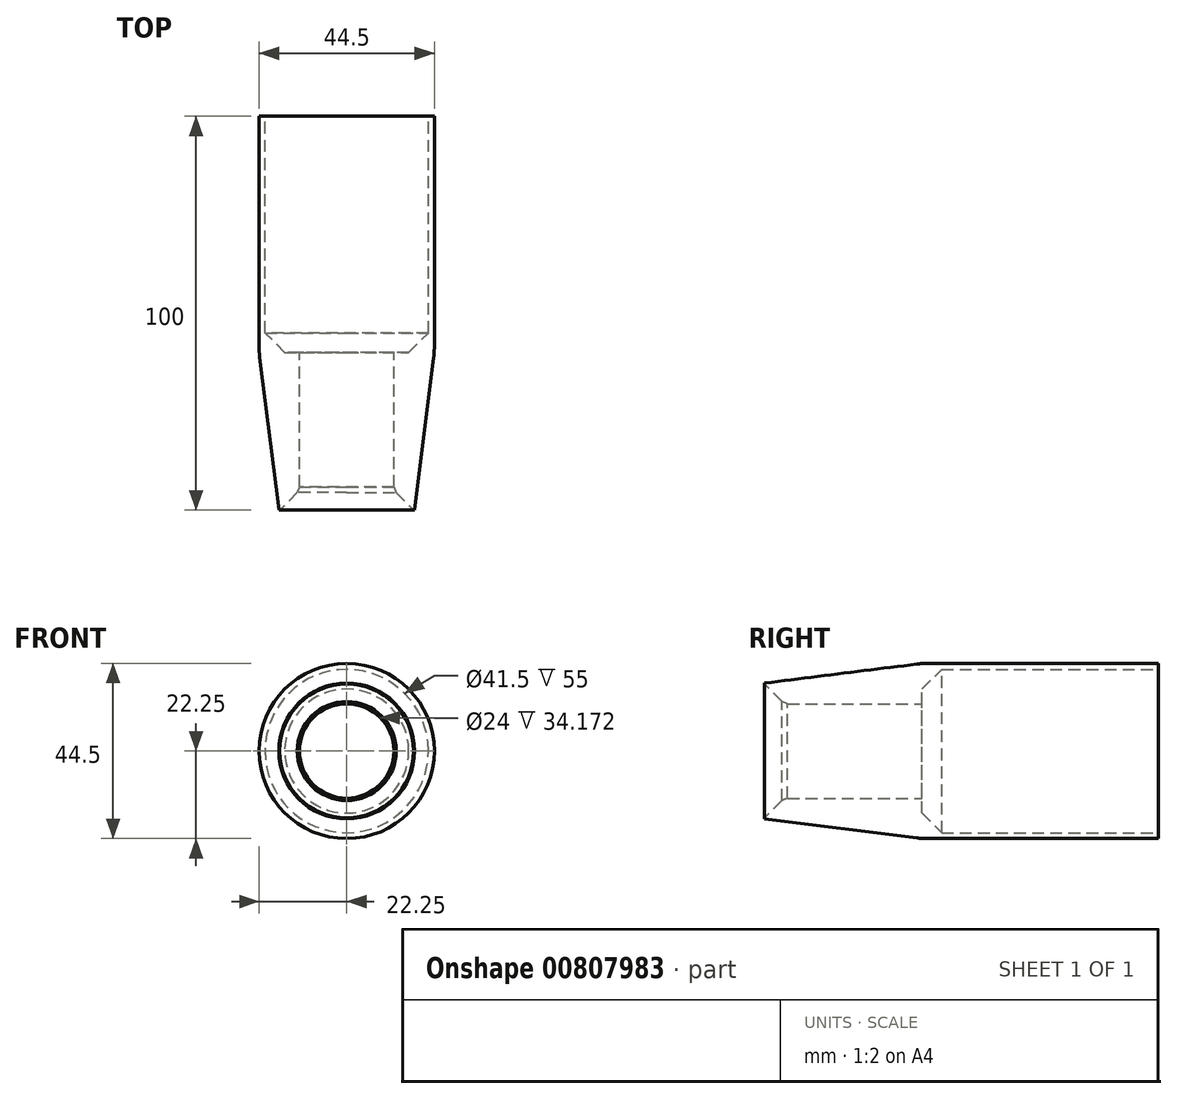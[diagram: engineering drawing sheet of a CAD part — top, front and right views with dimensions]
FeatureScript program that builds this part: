
annotation { "Feature Type Name" : "Feature", "Feature Type Description" : "" }
export const myFeature = defineFeature(function(context is Context, id is Id, definition is map)
    precondition{}
    {
        {
            var Q0;
            Q0=qCreatedBy(makeId("Front.planeOp"),FACE);
            var sketch = newSketch(context, id + "F0", { "sketchPlane" : qUnion([Q0])});
            skCircle(sketch, "E0", {"center": v(0, 0) * mm, "radius": 22.25 * mm});
            skSolve(sketch);
        }
        {
            var Q0;
            Q0 = qSketchRegion(id + "F0", true);
            extrude(context, id + "F1", {"entities" : qUnion([Q0]), "depth" : 100 * mm, "offsetDistance" : 25 * mm});
        }
        {
            var Q0;
            Q0=qCreatedBy(makeId("Front.planeOp"),FACE);
            var sketch = newSketch(context, id + "F2", { "sketchPlane" : qUnion([Q0])});
            skCircle(sketch, "E1", {"center": v(0, 0) * mm, "radius": 20.75 * mm});
            skSolve(sketch);
        }
        {
            var Q0;
            Q0 = qSketchRegion(id + "F2", true);
            extrude(context, id + "F3", {"entities" : qUnion([Q0]), "operationType" : NewBodyOperationType.REMOVE, "depth" : 60 * mm, "offsetDistance" : 25 * mm});
        }
        {
            var Q0;
            Q0=qCreatedBy(makeId("Front.planeOp"),FACE);
            var sketch = newSketch(context, id + "F4", { "sketchPlane" : qUnion([Q0])});
            skCircle(sketch, "E2", {"center": v(0, 0) * mm, "radius": 12 * mm});
            skSolve(sketch);
        }
        {
            var Q0;
            Q0=makeQuery(id+"F4.imprint","IMPRINT",FACE,{"disambiguationData":[TD([[makeQuery(id+"F4.imprint","IMPRINT",EDGE,{"derivedFrom":sQuery(id+"F4.wireOp",EDGE,"E2")}),1.0]])]});
            extrude(context, id + "F5", {"entities" : qUnion([Q0]), "operationType" : NewBodyOperationType.REMOVE, "depth" : 191.6 * mm, "offsetDistance" : 25 * mm});
        }
        {
            var Q0;
            Q0=makeQuery(id+"F1.opExtrude","CAP_EDGE",EDGE,{"disambiguationData":[OSD([sQuery(id+"F0.wireOp",EDGE,"E0")])],"isStart":false});
            chamfer(context, id + "F6", {"entities" : qUnion([Q0]), "chamferType" : ChamferType.TWO_OFFSETS, "width1" : 5 * mm, "oppositeDirection" : false, "width2" : 40 * mm});
        }
        {
            var Q0;
            Q0=makeQuery(id+"F3.boolean.opBoolean","COPY",EDGE,{"derivedFrom":makeQuery(id+"F3.opExtrude","CAP_EDGE",EDGE,{"disambiguationData":[OSD([sQuery(id+"F2.wireOp",EDGE,"E1")])],"isStart":false})});
            var Q1;
            Q1=makeQuery(id+"F5.boolean.opBoolean","INTERSECT",EDGE,{"derivedFrom":[makeQuery(id+"F1.opExtrude","CAP_FACE",FACE,{"disambiguationData":[OSD([sQuery(id+"F0.wireOp",EDGE,"E0")])],"isStart":false}),makeQuery(id+"F5.opExtrude","SWEPT_FACE",FACE,{"disambiguationData":[OSD([sQuery(id+"F4.wireOp",EDGE,"E2")])]})]});
            chamfer(context, id + "F7", {"entities" : qUnion([Q0, Q1]), "width" : 5 * mm, "tangentPropagation" : true});
        }
        {
            var Q0;
            {var subQ0=sQuery(id+"F0.wireOp",EDGE,"E0");Q0=makeQuery(id+"F6.opChamfer","BLEND_EDGE",EDGE,{"blendedFrom":[makeQuery(id+"F1.opExtrude","CAP_EDGE",EDGE,{"disambiguationData":[OSD([subQ0])],"isStart":false}),makeQuery(id+"F1.opExtrude","SWEPT_FACE",FACE,{"disambiguationData":[OSD([subQ0])]})],"blendedInto":[makeQuery(id+"F1.opExtrude","SWEPT_FACE",FACE,{"disambiguationData":[OSD([subQ0])]})]});}
            fillet(context, id + "F8", {"entities" : qUnion([Q0]), "radius" : 20 * mm, "tangentPropagation" : true, "allowEdgeOverflow" : false});
        }
        {
            var Q0;
            Q0=makeQuery(id+"F3.boolean.opBoolean","COPY",EDGE,{"derivedFrom":makeQuery(id+"F3.opExtrude","CAP_EDGE",EDGE,{"disambiguationData":[OSD([sQuery(id+"F2.wireOp",EDGE,"E1")])],"isStart":true})});
            var Q1;
            {var subQ0=makeQuery(id+"F5.opExtrude","SWEPT_FACE",FACE,{"disambiguationData":[OSD([sQuery(id+"F4.wireOp",EDGE,"E2")])]});Q1=makeQuery(id+"F7.opChamfer","BLEND_EDGE",EDGE,{"blendedFrom":[makeQuery(id+"F5.boolean.opBoolean","INTERSECT",EDGE,{"derivedFrom":[makeQuery(id+"F1.opExtrude","CAP_FACE",FACE,{"disambiguationData":[OSD([sQuery(id+"F0.wireOp",EDGE,"E0")])],"isStart":false}),subQ0]}),makeQuery(id+"F5.boolean.opBoolean","COPY",FACE,{"derivedFrom":subQ0})],"blendedInto":[makeQuery(id+"F5.boolean.opBoolean","COPY",FACE,{"derivedFrom":subQ0})]});}
            chamfer(context, id + "F9", {"entities" : qUnion([Q0, Q1]), "width" : 2 * mm, "tangentPropagation" : true});
        }
    });
